# Revit family: Sanitary_Taps-Mixers_AXOR_36108CHN-AXOR-Citterio-E-3-hole-basin-mi_10
name_source: partatom
category: Plumbing Fixtures
revit_build: Autodesk Revit 2018 (Build: 20170223_1515(x64)
units: mm (PartAtom-declared; Revit-internal decimal feet)

## family parameters
Always vertical = No
Cut with Voids When Loaded = No
OmniClass Number = 23.31.11.00
OmniClass Title = Faucets
Part Type = Normal
Room Calculation Point = No
Round Connector Dimension = Use Diameter
Shared = No
Work Plane-Based = Yes

## types (4) — shared parameters
Always visible = Yes
BIMobject category = Taps & Mixers
Connector Description = Water Inlet 12.7mm
Default Elevation = 1219.2 mm  [stored 4 ft]
Description = AXOR Citterio E 3-hole basin mixer 170 with escutcheons and pop-up waste set
Design country = Germany
Diameter = 12.7 mm  [stored 0.0416667 ft]
EAN code = 4059625427347
Edition number = 1
GTIN code = https://4059625427347
IFC Classification = Valve
Manufacturer country = Germany
Manufacturer name = AXOR
Model = 36108CHN
OmniClass Code = 23-31 11 00
OmniClass Description = Faucets
Product Guid = b0d75d61-537f-4fa6-a7d6-d060741bdd7c
Product SKU = 36108CHN
Product data url = https://bimobject.com
Product family = AXOR Citterio E
Product group = Basin mixers
Product name = 36108CHN AXOR Citterio E 3-hole basin mixer 170 with escutcheons and pop-up waste set
QR code = https://bimobject.com
URL = https://www.axor-design.com
Weight Net (Kg) = 3.2

## per-type parameters (varying)
| type | Manufacturer | Material 1 |
| 997 Polished Gold Optic | AXOR
AXOR
AXOR | AXOR - Metal - 997 Polished Gold Optic |
| 677 Matt Black | AXOR | AXOR - Metal - 677 Matt Black |
| 347 Brushed Black Chrome | AXOR | AXOR - Metal - 347 Brushed Black Chrome |
| 007 Chrome | AXOR | AXOR - Metal - 007 Chrome |

note: [stored X ft] marks values corroborated as IEEE doubles in the binary element streams (Revit-internal decimal feet)

## geometry (parser evidence)
native form markers: Sweep x2
no freeform markers — native parametric forms only
